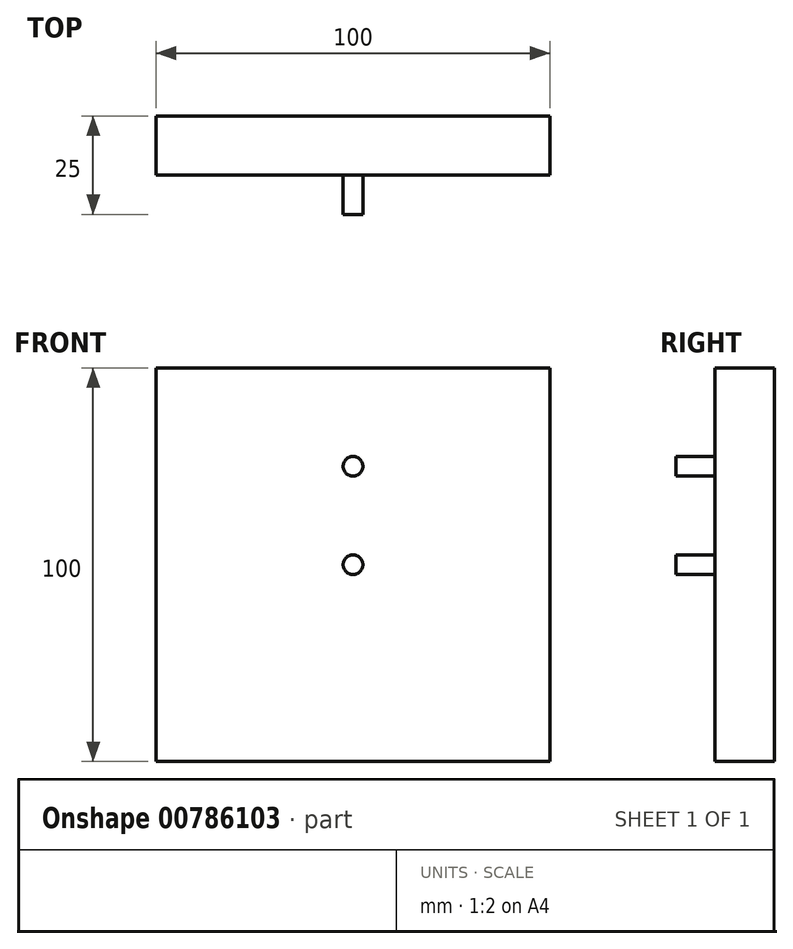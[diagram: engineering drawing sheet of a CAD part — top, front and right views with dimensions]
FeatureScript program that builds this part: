
annotation { "Feature Type Name" : "Feature", "Feature Type Description" : "" }
export const myFeature = defineFeature(function(context is Context, id is Id, definition is map)
    precondition{}
    {
        {
            var Q0;
            Q0=qCreatedBy(makeId("Front.planeOp"),FACE);
            var sketch = newSketch(context, id + "F0", { "sketchPlane" : qUnion([Q0])});
            skLineSegment(sketch, "E0.bottom", {"start": v(50, -50) * mm, "end": v(-50, -50) * mm});
            skLineSegment(sketch, "E0.top", {"start": v(50, 50) * mm, "end": v(-50, 50) * mm});
            skLineSegment(sketch, "E0.left", {"start": v(50, -50) * mm, "end": v(50, 50) * mm});
            skLineSegment(sketch, "E0.right", {"start": v(-50, -50) * mm, "end": v(-50, 50) * mm});
            skPoint(sketch, "E0.middle", {"position": v(0, 0) * mm});
            skSolve(sketch);
        }
        {
            var Q0;
            Q0=makeQuery(id+"F0.imprint","IMPRINT",FACE,{"disambiguationData":[TD([[makeQuery(id+"F0.imprint","IMPRINT",EDGE,{"derivedFrom":sQuery(id+"F0.wireOp",EDGE,"E0.bottom")}),-1.0]])]});
            extrude(context, id + "F1", {"entities" : qUnion([Q0]), "oppositeDirection" : true, "depth" : 15 * mm, "offsetDistance" : 25 * mm});
        }
        {
            var Q0;
            Q0=makeQuery(id+"F1.opExtrude","CAP_FACE",FACE,{"disambiguationData":[OSD([sQuery(id+"F0.wireOp",EDGE,"E0.bottom"),sQuery(id+"F0.wireOp",EDGE,"E0.top"),sQuery(id+"F0.wireOp",EDGE,"E0.left"),sQuery(id+"F0.wireOp",EDGE,"E0.right")])],"isStart":true});
            var sketch = newSketch(context, id + "F2", { "sketchPlane" : qUnion([Q0])});
            skCircle(sketch, "E1", {"center": v(0, 0) * mm, "radius": 2.5 * mm});
            skLineSegment(sketch, "E2", {"start": v(0, 0) * mm, "end": v(0, 25) * mm, "construction": true});
            skCircle(sketch, "E3", {"center": v(0, 25) * mm, "radius": 2.5 * mm});
            skSolve(sketch);
        }
        {
            var Q0;
            Q0 = qSketchRegion(id + "F2", true);
            extrude(context, id + "F3", {"entities" : qUnion([Q0]), "operationType" : NewBodyOperationType.ADD, "depth" : 10 * mm, "offsetDistance" : 25 * mm});
        }
    });
